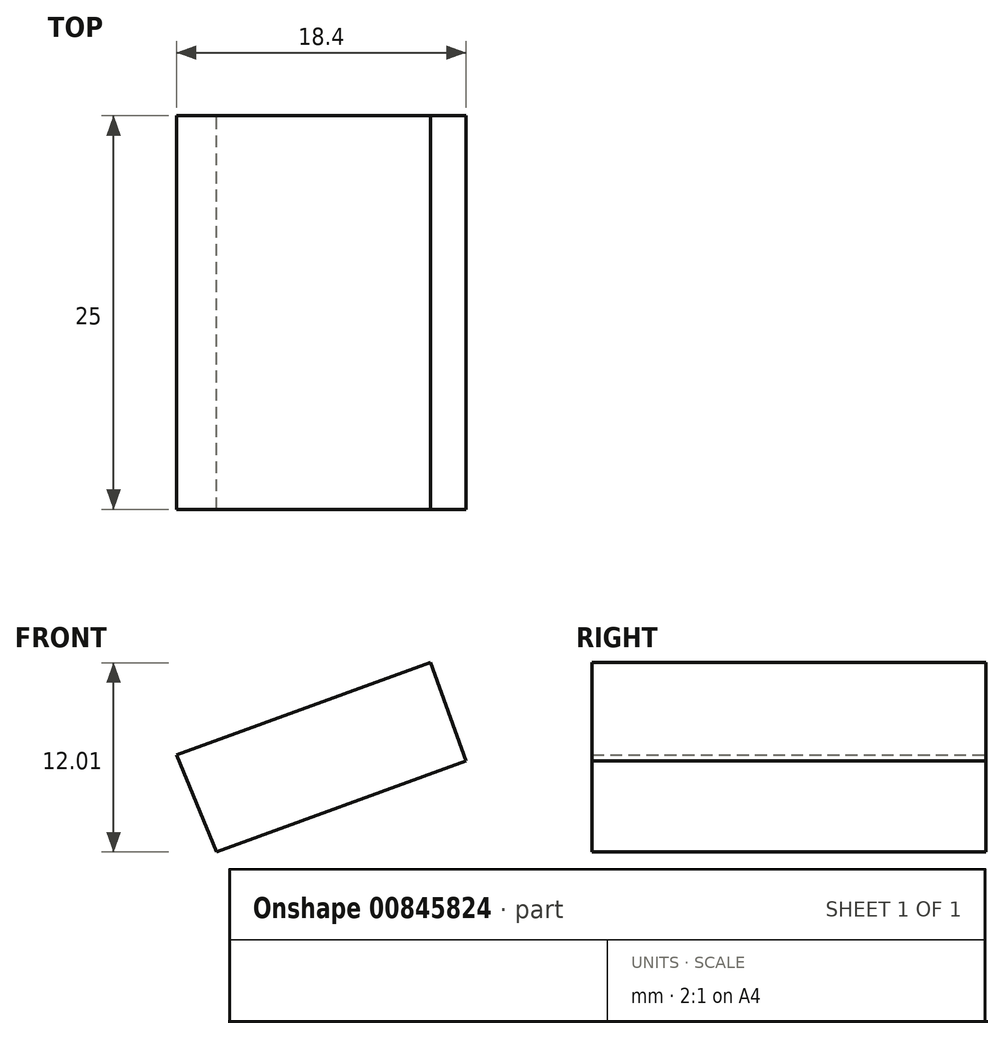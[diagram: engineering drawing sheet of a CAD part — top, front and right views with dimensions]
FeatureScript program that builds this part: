
annotation { "Feature Type Name" : "Feature", "Feature Type Description" : "" }
export const myFeature = defineFeature(function(context is Context, id is Id, definition is map)
    precondition{}
    {
        {
            var Q0;
            Q0=qCreatedBy(makeId("Front.planeOp"),FACE);
            var sketch = newSketch(context, id + "F0", { "sketchPlane" : qUnion([Q0])});
            skLineSegment(sketch, "E0", {"start": v(-66.56, -14.4) * mm, "end": v(-39.67, -14.4) * mm});
            skLineSegment(sketch, "E1", {"start": v(-66.56, -14.4) * mm, "end": v(-38.45, -4.17) * mm});
            skLineSegment(sketch, "E2", {"start": v(-50.71, -8.64) * mm, "end": v(-52.98, -2.4) * mm});
            skLineSegment(sketch, "E3", {"start": v(-52.98, -2.4) * mm, "end": v(-69.1, -8.26) * mm});
            skLineSegment(sketch, "E4", {"start": v(-69.1, -8.26) * mm, "end": v(-66.56, -14.4) * mm});
            skLineSegment(sketch, "E5", {"start": v(-50.71, -8.64) * mm, "end": v(-50.71, -21.6) * mm});
            skLineSegment(sketch, "E6", {"start": v(-66.56, -14.4) * mm, "end": v(-66.56, -22.35) * mm});
            skSolve(sketch);
        }
        {
            var Q0;
            {var subQ2=sQuery(id+"F0.wireOp",EDGE,"E2");Q0=makeQuery(id+"F0.imprint","IMPRINT",FACE,{"disambiguationData":[TD([[makeQuery(id+"F0.imprint","IMPRINT",EDGE,{"derivedFrom":subQ2}),1.0]])]});}
            extrude(context, id + "F1", {"entities" : qUnion([Q0]), "depth" : 25 * mm, "offsetDistance" : 25 * mm});
        }
    });
